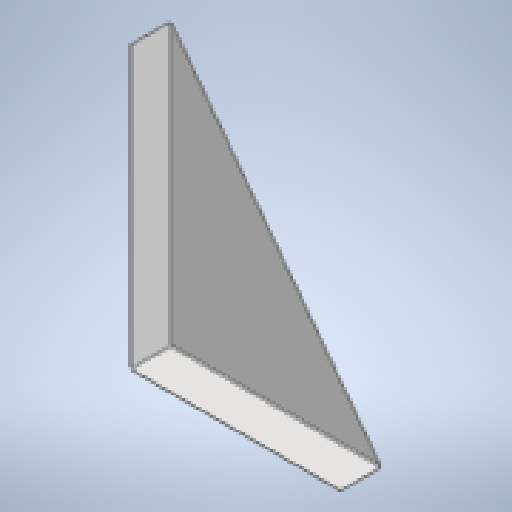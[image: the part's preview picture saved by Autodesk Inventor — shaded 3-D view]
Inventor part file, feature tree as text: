
AUTODESK INVENTOR PART (.ipt)
format: ipt  version: 2025.2 (Build 292293000, 293)  size: 174,592 bytes
history: native  units: mm
features: sheet_metal_op x4, other x3, sketch x2
ambient origin geometry x8: Origin, YZ Plane, XZ Plane, XY Plane, X Axis, Y Axis, Z Axis, Center Point
bodies: Solid1 (feature_tree)
feature tree (9):
  sheet_metal_op  "Face1"
  sheet_metal_op  "Flange1"
  sketch  "Sketch1"  dims[d0=76.2mm]
  other  "Plate1"
  sketch  "Sketch2"  dims[d1=120.65mm d2=0.5mm d3=0.5mm d4=0.25mm d5=1.0mm d6=0.5mm d7=15.0mm d8=90.0deg d9=0.5mm d10=2.0mm d11=0.5mm d12=0.5mm]
  other  "Plate2"
  sheet_metal_op  "Bend1"
  sheet_metal_op  "Corner1"
  other  "Definition1"
